FCSTD DOCUMENT  (FreeCAD 0.16R)
Label: Mk10
License: All rights reserved
LicenseURL: http://en.wikipedia.org/wiki/All_rights_reserved
objects: Sketcher::SketchObject×2
note: 2 computed .brp shape members not serialized (recipe doc carries the construction recipe); baked Part::Feature solids carry a one-line shape summary decoded from their .brp

FEATURE [Sketcher::SketchObject] Sketch
  sketch-geometry (16):
    g0: Circle CenterX=-195.689 CenterY=150 CenterZ=0 NormalX=0 NormalY=0 NormalZ=1 Radius=150
    g1: Circle CenterX=300 CenterY=150 CenterZ=0 NormalX=0 NormalY=0 NormalZ=1 Radius=150
    g2: Circle [constr] CenterX=0 CenterY=108.697 CenterZ=0 NormalX=0 NormalY=0 NormalZ=1 Radius=75
    g3: LineSegment StartX=-68.078 StartY=331.37 StartZ=0 EndX=0 EndY=108.697 EndZ=0
    g4: LineSegment StartX=0 StartY=108.697 StartZ=0 EndX=231.571 EndY=315.255 EndZ=0
    g5: LineSegment StartX=-195.689 StartY=150 StartZ=0 EndX=213.18 EndY=324.317 EndZ=0
    g6: LineSegment StartX=200.485 StartY=375.374 StartZ=0 EndX=276.224 EndY=142.275 EndZ=0
    g7: LineSegment StartX=260.9 StartY=310.787 StartZ=0 EndX=189.571 EndY=287.611 EndZ=0
    g8: LineSegment StartX=276.224 StartY=142.275 StartZ=0 EndX=300 EndY=150 EndZ=0
    g9: LineSegment StartX=210.22 StartY=304.313 StartZ=0 EndX=234.377 EndY=312.163 EndZ=0
    g10: LineSegment StartX=212.384 StartY=297.656 StartZ=0 EndX=236.54 EndY=305.505 EndZ=0
    g11: LineSegment StartX=186.735 StartY=376.594 StartZ=0 EndX=210.892 EndY=384.443 EndZ=0
    g12: LineSegment StartX=184.572 StartY=383.251 StartZ=0 EndX=208.729 EndY=391.1 EndZ=0
    g13: LineSegment [constr] StartX=191.629 StartY=366.709 StartZ=0 EndX=210.826 EndY=307.629 EndZ=0
    g14: LineSegment StartX=-195.689 StartY=150 StartZ=0 EndX=0 EndY=108.697 EndZ=0
    g15: LineSegment [constr] StartX=-195.689 StartY=150 StartZ=0 EndX=300 EndY=150 EndZ=0
  constraints (40):
    c: Radius(g0) = 150
    c: Equal(g0,g1)
    c: Tangent(g1,g-1)
    c: Tangent(g-1,g0)
    c: Radius(g2) = 75
    c: Coincident(g3,g2)
    c: Coincident(g4,g2)
    c: Angle(g3) = -1.27409
    c: Angle(g6) = -1.25664
    c: PointOnObject(g2,g-2)
    c: Perpendicular(g7,g6)
    c: Distance(g1,g7) = 165
    c: Coincident(g1,g8)
    c: Coincident(g8,g6)
    c: Perpendicular(g8,g6)
    c: Distance(g8) = 25
    c: Symmetric(g7,g7,g6)
    c: Distance(g7) = 75
    c: Distance(g9) = 25.4
    c: Symmetric(g9,g9,g6)
    c: Distance(g10,g9) = 7
    c: Parallel(g10,g9)
    c: Distance(g10) = 25.4
    c: Distance(g11) = 25.4
    c: Symmetric(g11,g11,g6)
    c: Parallel(g12,g11)
    c: Distance(g12) = 25.4
    c: Symmetric(g12,g12,g6)
    c: Distance(g11,g12) = 7
    c: Distance(g12,g10) = 90
    c: Symmetric(g10,g10,g6)
    c: Distance(g13,g6) = 11.1
    c: Distance(g13,g6) = 11.1
    c: DistanceX(g-2,g1) = 300
    c: Coincident(g14,g0)
    c: Coincident(g14,g2)
    c: Coincident(g15,g0)
    c: Coincident(g15,g1)
    c: Distance(g14) = 200
    c: Coincident(g0,g5)
FEATURE [Sketcher::SketchObject] Sketch001
  sketch-geometry (22):
    g0: LineSegment StartX=-20 StartY=191.1 StartZ=0 EndX=20 EndY=191.1 EndZ=0
    g1: LineSegment StartX=20 StartY=191.1 StartZ=0 EndX=20 EndY=168.9 EndZ=0
    g2: LineSegment StartX=20 StartY=168.9 StartZ=0 EndX=-20 EndY=168.9 EndZ=0
    g3: LineSegment StartX=-20 StartY=168.9 StartZ=0 EndX=-20 EndY=191.1 EndZ=0
    g4: LineSegment StartX=-37.5 StartY=11.0515 StartZ=0 EndX=-37.5 EndY=-8.23225 EndZ=0
    g5: LineSegment StartX=37.5 StartY=-4.97783 StartZ=0 EndX=37.5 EndY=11.0515 EndZ=0
    g6: Circle CenterX=0 CenterY=132 CenterZ=0 NormalX=0 NormalY=0 NormalZ=1 Radius=18
    g7: LineSegment [constr] StartX=-11.5892 StartY=150 StartZ=0 EndX=12.6958 EndY=150 EndZ=0
    g8: LineSegment StartX=24 StartY=195 StartZ=0 EndX=36.7 EndY=195 EndZ=0
    g9: LineSegment StartX=36.7 StartY=195 StartZ=0 EndX=36.7 EndY=75 EndZ=0
    g10: LineSegment StartX=24 StartY=165 StartZ=0 EndX=24 EndY=195 EndZ=0
    g11: LineSegment StartX=30.35 StartY=161.437 StartZ=0 EndX=30.35 EndY=75 EndZ=0
    g12: LineSegment StartX=30.35 StartY=75 StartZ=0 EndX=36.7 EndY=75 EndZ=0
    g13: LineSegment StartX=22 StartY=225 StartZ=0 EndX=24 EndY=225 EndZ=0
    g14: LineSegment StartX=24 StartY=225 StartZ=0 EndX=24 EndY=135 EndZ=0
    g15: LineSegment StartX=24 StartY=135 StartZ=0 EndX=22 EndY=135 EndZ=0
    g16: LineSegment StartX=22 StartY=135 StartZ=0 EndX=22 EndY=225 EndZ=0
    g17: LineSegment [constr] StartX=-44.8398 StartY=180 StartZ=0 EndX=55.9928 EndY=180 EndZ=0
    g18: LineSegment [constr] StartX=25 StartY=15.033 StartZ=0 EndX=25 EndY=-20.667 EndZ=0
    g19: LineSegment [constr] StartX=22.9651 StartY=179.857 StartZ=0 EndX=25 EndY=0 EndZ=0
    g20: LineSegment [constr] StartX=20.309 StartY=149.447 StartZ=0 EndX=21.999 EndY=0.0742734 EndZ=0
    g21: LineSegment [constr] StartX=27.9986 StartY=0.142152 StartZ=0 EndX=26.3121 EndY=149.208 EndZ=0
  constraints (57):
    c: Coincident(g0,g1)
    c: Coincident(g1,g2)
    c: Coincident(g2,g3)
    c: Coincident(g3,g0)
    c: Horizontal(g0)
    c: Horizontal(g2)
    c: Vertical(g1)
    c: Vertical(g3)
    c: Symmetric(g0,g0,g-2)
    c: Distance(g2) = 40
    c: Distance(g1) = 22.2
    c: Vertical(g4)
    c: Symmetric(g4,g5,g-2)
    c: Vertical(g5)
    c: Distance(g5,g4) = 75
    c: Radius(g6) = 18
    c: Horizontal(g7)
    c: Tangent(g6,g7)
    c: PointOnObject(g6,g-2)
    c: DistanceY(g7) = 150
    c: Coincident(g8,g9)
    c: Coincident(g10,g8)
    c: Horizontal(g8)
    c: Vertical(g9)
    c: Vertical(g10)
    c: Vertical(g11)
    c: Coincident(g12,g11)
    c: Horizontal(g12)
    c: Coincident(g12,g9)
    c: Distance(g10) = 30
    c: Distance(g9) = 120
    c: Coincident(g13,g14)
    c: Coincident(g14,g15)
    c: Coincident(g15,g16)
    c: Coincident(g16,g13)
    c: Horizontal(g13)
    c: Horizontal(g15)
    c: Vertical(g14)
    c: Vertical(g16)
    c: Distance(g14) = 90
    c: Symmetric(g2,g0,g17)
    c: DistanceY(g17) = 180
    c: Symmetric(g15,g13,g17)
    c: Distance(g13) = 2
    c: Distance(g12) = 6.35
    c: Distance(g8) = 12.7
    c: Distance(g1,g16) = 2
    c: Symmetric(g8,g10,g17)
    c: PointOnObject(g10,g14)
    c: Vertical(g18)
    c: DistanceX(g-2,g18) = 25
    c: PointOnObject(g19,g18)
    c: Parallel(g21,g19)
    c: Parallel(g20,g19)
    c: Symmetric(g20,g21,g19)
    c: Distance(g21,g20) = 6
    c: PointOnObject(g19,g-1)
